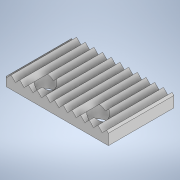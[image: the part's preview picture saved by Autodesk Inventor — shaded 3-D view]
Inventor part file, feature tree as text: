
AUTODESK INVENTOR PART (.ipt)
format: ipt  version: 2020 (Build 240168000, 168)  size: 264,192 bytes
history: native  units: in
note: dims shown in document units (in); Inventor stores cm internally (conversion verified against a paired STEP export)
features: extrude x4, sketch x4
ambient origin geometry x8: Origin, YZ Plane, XZ Plane, XY Plane, X Axis, Y Axis, Z Axis, Center Point
bodies: Solid1 (feature_tree)
feature tree (8):
  extrude  "Extrusion1"  Depth=0.6299in
  extrude  "Extrusion2"  Depth=0.0591in
  extrude  "Extrusion4"  TaperAngle=45.0deg  [1 undecoded]
  extrude  "Extrusion5"  Depth=0.0591in
  sketch  "Sketch1"  dims[d0=1.8898in d1=0.6299in]
  sketch  "Sketch2"  dims[d2=0.0787in d3=0.0in d6=0.0591in]
  sketch  "Sketch4"  dims[d7=0.0591in d8=45.0deg]
  sketch  "Sketch5"  dims[d9=0.0591in d10=0.0591in d11=90.0deg d12=0.0591in d13=0.0591in d14=0.0591in d15=0.0591in d16=45.0deg d17=0.0591in d18=90.0deg d19=0.0591in d20=0.0591in d21=0.0591in d22=0.0591in d23=0.0591in d24=0.0591in d25=90.0deg d26=0.0591in d27=90.0deg d28=0.0591in d29=90.0deg d30=0.0591in d31=0.0591in d32=0.0591in d33=0.0591in d34=90.0deg d35=0.0591in d36=90.0deg d37=0.0591in d38=90.0deg d39=0.0591in d40=90.0deg d41=0.0591in d42=90.0deg d43=0.0591in d44=90.0deg d45=0.0591in d46=45.0deg d47=0.0591in d48=90.0deg d49=0.0591in d50=90.0deg d51=0.0591in d52=90.0deg d53=0.0591in d54=90.0deg d55=0.0591in d56=90.0deg d57=0.0591in d58=90.0deg d59=0.0591in d60=90.0deg d61=0.0591in d62=90.0deg d63=0.0591in d64=90.0deg d65=0.0591in d66=90.0deg d67=0.0591in d68=90.0deg d69=0.0591in d70=90.0deg d71=0.0591in d72=90.0deg d73=0.0591in d74=90.0deg d75=0.0591in d76=90.0deg d77=0.0591in d78=90.0deg d79=0.0591in d80=90.0deg d81=0.0591in d82=90.0deg d83=0.0591in d84=90.0deg d85=0.6299in d86=0.0in d93=0.9843in d94=0.6299in d95=0.3937in d96=0.0in d97=0.1575in d98=0.1575in d99=0.3937in d100=0.0in]
note: 1 required parameter value undecoded (feature->parameter linkage not recoverable at this tier; creation-order binding heuristic only, values carry confidence <= 0.55)
